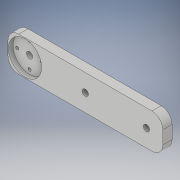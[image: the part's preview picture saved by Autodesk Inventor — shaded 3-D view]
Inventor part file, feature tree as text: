
AUTODESK INVENTOR PART (.ipt)
format: ipt  version: 2019 (Build 230136000, 136)  size: 142,848 bytes
history: native  units: mm
features: extrude x4, sketch x4, other x1, fillet x1
ambient origin geometry x8: Origin, YZ Plane, XZ Plane, XY Plane, X Axis, Y Axis, Z Axis, Center Point
bodies: Body1 (feature_tree)
feature tree (10):
  other  "Твердое тело1"
  extrude  "Выдавливание1"  Depth=100.0mm
  extrude  "Выдавливание2"  Depth=22.5mm
  extrude  "Выдавливание3"  Depth=10.5mm
  fillet  "Сопряжение1"  Radius=11.0mm
  extrude  "Выдавливание4"  Depth=21.0mm
  sketch  "Эскиз1"
  sketch  "Эскиз2"
  sketch  "Эскиз3"
  sketch  "Эскиз4"
